# Revit family: 306_6f76f4a0bab145aa8465ba9f9c5a91
name_source: partatom
category: Pipe Accessories
units: mm (PartAtom-declared; Revit-internal decimal feet)

## family parameters
Always vertical = Yes
Cut with Voids When Loaded = No
Part Type = Valve - Breaks Into
Round Connector Dimension = Use Diameter
Shared = No
Work Plane-Based = No

## types (15) — shared parameters
Description = 2-port valve, female thread, PN16, DN15-50, Kvs0.6-39
H3 = 30 mm  [stored 0.0984252 ft]
H4 = 45 mm  [stored 0.147638 ft]
H4__ve = -45 mm  [stored -0.147638 ft]
L2D = 70 mm
L2D_Min = 3048 mm
Manufacturer = Regin
QmdConnectorList = 301;D;302;D
R5 = 24 mm
R7 = 13 mm
URL = https://www.regincontrols.com
W2D = 15 mm  [stored 0.0492126 ft]
magiPartTypeId = 306
magiProductFamilyId = 6f76f4a0bab145aa8465ba9f9c5a91

## per-type parameters (varying)
| type | CenSd_NV_6 | D | H | L1 | L1__ve | L_2 | NV | R1 | R2 | R3 | R4 | magiProductId |
| BTV15-0,6 | 15 mm  [stored 0.0492126 ft] | 15 mm | 90 mm | 12 mm  [stored 0.0393701 ft] | -12 mm  [stored -0.0393701 ft] | 35 mm | 18 mm | 14 mm  [stored 0.0459318 ft] | 8 mm  [stored 0.0262467 ft] | 16 mm  [stored 0.0524934 ft] | 17 mm  [stored 0.0557743 ft] | de996625c75b4fb2b10fc663aca436 |
| BTV15-1,0 | 15 mm  [stored 0.0492126 ft] | 15 mm | 90 mm | 12 mm  [stored 0.0393701 ft] | -12 mm  [stored -0.0393701 ft] | 35 mm | 18 mm | 14 mm  [stored 0.0459318 ft] | 8 mm  [stored 0.0262467 ft] | 16 mm  [stored 0.0524934 ft] | 17 mm  [stored 0.0557743 ft] | d0504bd1734345da99f0087996de24 |
| BTV15-1,6 | 15 mm  [stored 0.0492126 ft] | 15 mm | 90 mm | 12 mm  [stored 0.0393701 ft] | -12 mm  [stored -0.0393701 ft] | 35 mm | 18 mm | 14 mm  [stored 0.0459318 ft] | 8 mm  [stored 0.0262467 ft] | 16 mm  [stored 0.0524934 ft] | 17 mm  [stored 0.0557743 ft] | 2efc24b42f674e42a8aa4985ad11fc |
| BTV15-2,5 | 15 mm  [stored 0.0492126 ft] | 15 mm | 90 mm | 12 mm  [stored 0.0393701 ft] | -12 mm  [stored -0.0393701 ft] | 35 mm | 18 mm | 14 mm  [stored 0.0459318 ft] | 8 mm  [stored 0.0262467 ft] | 16 mm  [stored 0.0524934 ft] | 17 mm  [stored 0.0557743 ft] | 4985c8776a324bdab210e34d15f83f |
| BTV20-1,6 | 19 mm | 20 mm | 90 mm | 14 mm  [stored 0.0459318 ft] | -14 mm | 38 mm | 21 mm | 17 mm  [stored 0.0557743 ft] | 6 mm  [stored 0.019685 ft] | 16 mm  [stored 0.0524934 ft] | 17 mm  [stored 0.0557743 ft] | 574af087fd2a4d31a7f524fd7427c2 |
| BTV20-2,7 | 19 mm | 20 mm | 90 mm | 14 mm  [stored 0.0459318 ft] | -14 mm | 38 mm | 21 mm | 17 mm  [stored 0.0557743 ft] | 6 mm  [stored 0.019685 ft] | 16 mm  [stored 0.0524934 ft] | 17 mm  [stored 0.0557743 ft] | ab12b09dfd204c5ebad12d9c3cf6bb |
| BTV25-10 | 22 mm  [stored 0.0721785 ft] | 25 mm | 104 mm | 15 mm  [stored 0.0492126 ft] | -15 mm | 45 mm  [stored 0.147638 ft] | 25 mm  [stored 0.082021 ft] | 20 mm  [stored 0.0656168 ft] | 11 mm | 22 mm  [stored 0.0721785 ft] | 24 mm | 312ea5734eb846adb2ea42a974b275 |
| BTV25-6,3 | 22 mm  [stored 0.0721785 ft] | 25 mm | 104 mm | 15 mm  [stored 0.0492126 ft] | -15 mm | 45 mm  [stored 0.147638 ft] | 25 mm  [stored 0.082021 ft] | 20 mm  [stored 0.0656168 ft] | 11 mm | 22 mm  [stored 0.0721785 ft] | 24 mm | 428e16127d42468bb2eaf6243c517d |
| BTV32-10 | 27 mm | 32 mm | 104 mm | 18 mm | -18 mm | 53 mm | 31 mm | 25 mm  [stored 0.082021 ft] | 5 mm  [stored 0.0164042 ft] | 22 mm  [stored 0.0721785 ft] | 17 mm  [stored 0.0557743 ft] | 61cdf942cab2406ba7d00f503d4c3f |
| BTV32-16 | 27 mm | 32 mm | 104 mm | 18 mm | -18 mm | 53 mm | 31 mm | 25 mm  [stored 0.082021 ft] | 5 mm  [stored 0.0164042 ft] | 22 mm  [stored 0.0721785 ft] | 17 mm  [stored 0.0557743 ft] | 87e49a4f3bbd474892d80e2bef7cfb |
| BTV40-16 | 30 mm  [stored 0.0984252 ft] | 40 mm | 120 mm | 19 mm | -19 mm | 60 mm | 35 mm | 29 mm | 15 mm  [stored 0.0492126 ft] | 22 mm  [stored 0.0721785 ft] | 17 mm  [stored 0.0557743 ft] | 0520f41068204585a3c2349e149136 |
| BTV40-27 | 30 mm  [stored 0.0984252 ft] | 40 mm | 120 mm | 19 mm | -19 mm | 60 mm | 35 mm | 29 mm | 15 mm  [stored 0.0492126 ft] | 22 mm  [stored 0.0721785 ft] | 17 mm  [stored 0.0557743 ft] | b0443992f4404bd3884ec9eddd5b90 |
| BTV50-27 | 36 mm | 50 mm | 124 mm | 22 mm  [stored 0.0721785 ft] | -22 mm | 73 mm | 42 mm | 35 mm | 10 mm  [stored 0.0328084 ft] | 22 mm  [stored 0.0721785 ft] | 17 mm  [stored 0.0557743 ft] | 5a72120fc4d44e0ab6f58624b3d252 |
| BTV50-39 | 36 mm | 50 mm | 124 mm | 22 mm  [stored 0.0721785 ft] | -22 mm | 73 mm | 42 mm | 35 mm | 10 mm  [stored 0.0328084 ft] | 22 mm  [stored 0.0721785 ft] | 17 mm  [stored 0.0557743 ft] | 8b2a587513bf46888000d045b1aa1a |
| BTV20-3,9 | 19 mm | 20 mm | 90 mm | 14 mm  [stored 0.0459318 ft] | -14 mm | 38 mm | 21 mm | 17 mm  [stored 0.0557743 ft] | 6 mm  [stored 0.019685 ft] | 16 mm  [stored 0.0524934 ft] | 17 mm  [stored 0.0557743 ft] | d4bd14b5557c4dae862155fd1d42b3 |

note: column(s) folded — value = type name in every type: MC Product Code

note: [stored X ft] marks values corroborated as IEEE doubles in the binary element streams (Revit-internal decimal feet)

## geometry (parser evidence)
native form markers: Sweep x2
no freeform markers — native parametric forms only
